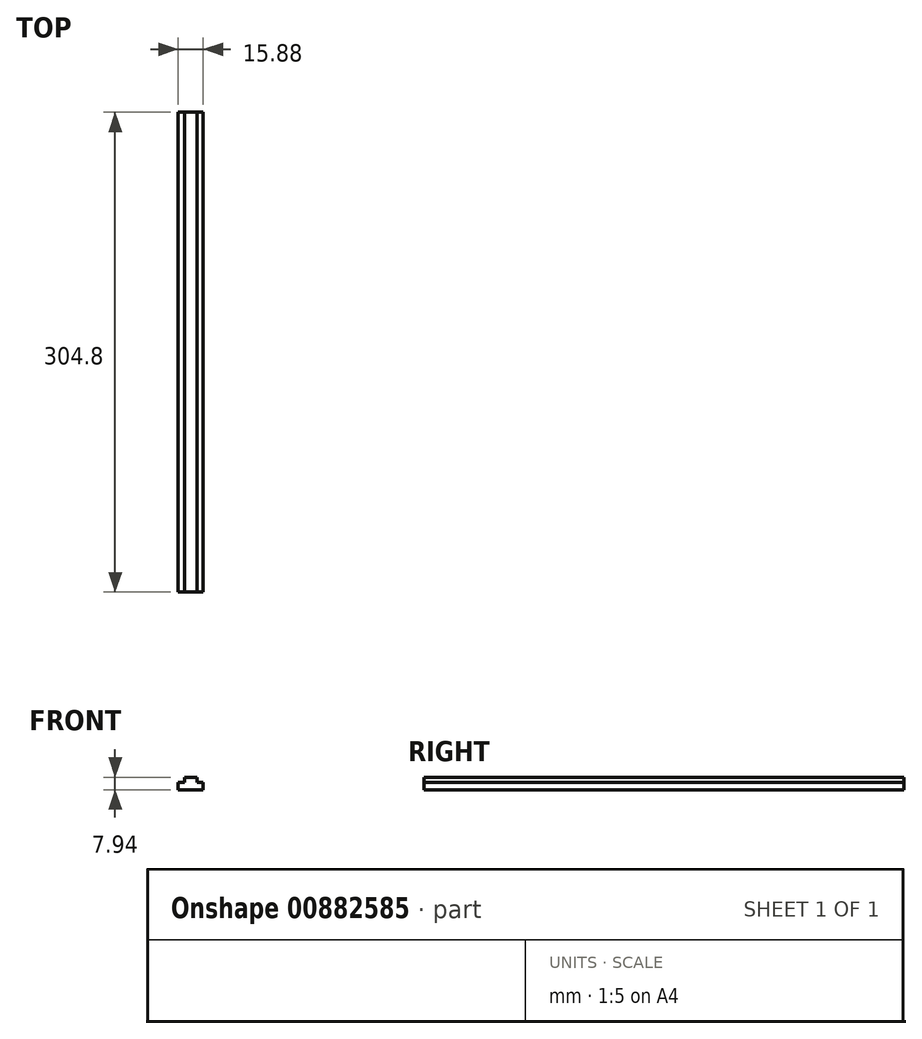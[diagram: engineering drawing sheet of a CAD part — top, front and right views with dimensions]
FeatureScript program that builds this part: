
annotation { "Feature Type Name" : "Feature", "Feature Type Description" : "" }
export const myFeature = defineFeature(function(context is Context, id is Id, definition is map)
    precondition{}
    {
        {
            var Q0;
            Q0=qCreatedBy(makeId("Front.planeOp"),FACE);
            var sketch = newSketch(context, id + "F0", { "sketchPlane" : qUnion([Q0])});
            skLineSegment(sketch, "E0", {"start": v(0, 0) * mm, "end": v(7.94, 0) * mm});
            skLineSegment(sketch, "E1", {"start": v(7.94, 0) * mm, "end": v(7.94, 4.76) * mm});
            skLineSegment(sketch, "E2", {"start": v(0, 0) * mm, "end": v(0, 7.94) * mm});
            skLineSegment(sketch, "E3", {"start": v(0, 7.94) * mm, "end": v(3.97, 7.94) * mm});
            skLineSegment(sketch, "E4", {"start": v(3.97, 7.94) * mm, "end": v(3.97, 4.76) * mm});
            skLineSegment(sketch, "E5", {"start": v(3.97, 4.76) * mm, "end": v(7.94, 4.76) * mm});
            skLineSegment(sketch, "E6.MirrorCS", {"start": v(0, 0) * mm, "end": v(-7.94, 0) * mm});
            skLineSegment(sketch, "E7.MirrorCS", {"start": v(-7.94, 0) * mm, "end": v(-7.94, 4.76) * mm});
            skLineSegment(sketch, "E8.MirrorCS", {"start": v(-3.97, 4.76) * mm, "end": v(-7.94, 4.76) * mm});
            skLineSegment(sketch, "E9.MirrorCS", {"start": v(-3.97, 7.94) * mm, "end": v(-3.97, 4.76) * mm});
            skLineSegment(sketch, "E10.MirrorCS", {"start": v(0, 7.94) * mm, "end": v(-3.97, 7.94) * mm});
            skSolve(sketch);
        }
        {
            var Q0;
            Q0=sQuery(id+"F0.wireOp",EDGE,"E6.MirrorCS");
            var Q1;
            Q1=sQuery(id+"F0.wireOp",EDGE,"E0");
            var Q2;
            Q2=sQuery(id+"F0.wireOp",EDGE,"E1");
            var Q3;
            Q3=sQuery(id+"F0.wireOp",EDGE,"E5");
            var Q4;
            Q4=sQuery(id+"F0.wireOp",EDGE,"E4");
            var Q5;
            Q5=sQuery(id+"F0.wireOp",EDGE,"E3");
            var Q6;
            Q6=sQuery(id+"F0.wireOp",EDGE,"E10.MirrorCS");
            var Q7;
            Q7=sQuery(id+"F0.wireOp",EDGE,"E9.MirrorCS");
            var Q8;
            Q8=sQuery(id+"F0.wireOp",EDGE,"E8.MirrorCS");
            var Q9;
            Q9=sQuery(id+"F0.wireOp",EDGE,"E7.MirrorCS");
            extrude(context, id + "F1", {"bodyType" : ToolBodyType.SURFACE, "surfaceEntities" : qUnion([Q0, Q1, Q2, Q3, Q4, Q5, Q6, Q7, Q8, Q9]), "depth" : 304.8 * mm, "offsetDistance" : 25.4 * mm});
        }
    });
